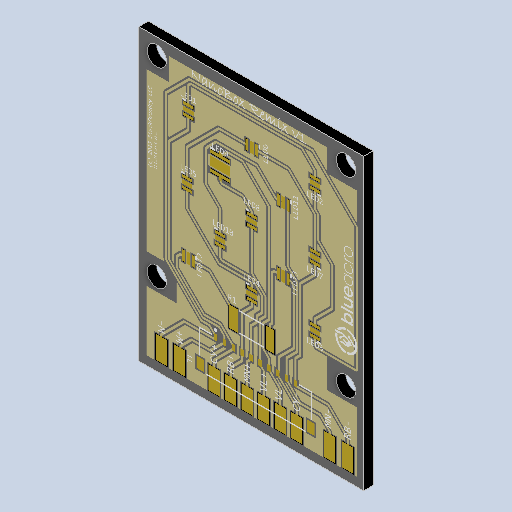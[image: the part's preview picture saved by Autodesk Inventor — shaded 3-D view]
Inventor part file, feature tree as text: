
AUTODESK INVENTOR PART (.ipt)
format: ipt  version: 2023.2 (Build 272271030, 271C)  size: 425,472 bytes
history: native  units: in
note: dims shown in document units (in); Inventor stores cm internally (conversion verified against a paired STEP export)
features: other x8, hole x4, sketch x4, extrude x1
ambient origin geometry x8: Origin, YZ Plane, XZ Plane, XY Plane, X Axis, Y Axis, Z Axis, Center Point
bodies: Solid1 (feature_tree)
feature tree (17):
  other  "nanobox_v31_upgrade_BOARD"
  other  "BoardFrontPlane"
  extrude  "BoardOutline"  Depth=0.0628in
  other  "Decal_Top"
  other  "Decal_Bottom"
  hole  "Free-18"  [1 undecoded]
  hole  "Free-19"  [1 undecoded]
  hole  "Free-17"  [1 undecoded]
  hole  "Free-16"  [1 undecoded]
  other  "img_Top"
  other  "G_2134424113_TopDecalImage"
  other  "img_Bottom"
  other  "G_2134424113_BottomDecalImage"
  sketch  "Sketch4"  dims[d0=0.0628in d1=0.0in d2=0.0628in]
  sketch  "Sketch5"  dims[d4=-0.0628in]
  sketch  "Sketch6"  dims[d6=0.1285in d7=0.75in d8=0.375in d9=0.25in d10=0.5635in d11=1.0in d12=0.0in]
  sketch  "Sketch7"  dims[d13=0.1285in d14=0.75in d15=0.375in d16=0.25in d17=0.5635in d18=1.0in d19=0.0in d20=0.1285in d21=0.75in d22=0.375in d23=0.25in d24=0.5635in d25=1.0in d26=0.0in d27=0.1285in d28=0.75in d29=0.375in d30=0.25in d31=0.5635in d32=1.0in d33=0.0in]
note: 4 required parameter values undecoded (feature->parameter linkage not recoverable at this tier; creation-order binding heuristic only, values carry confidence <= 0.55)
